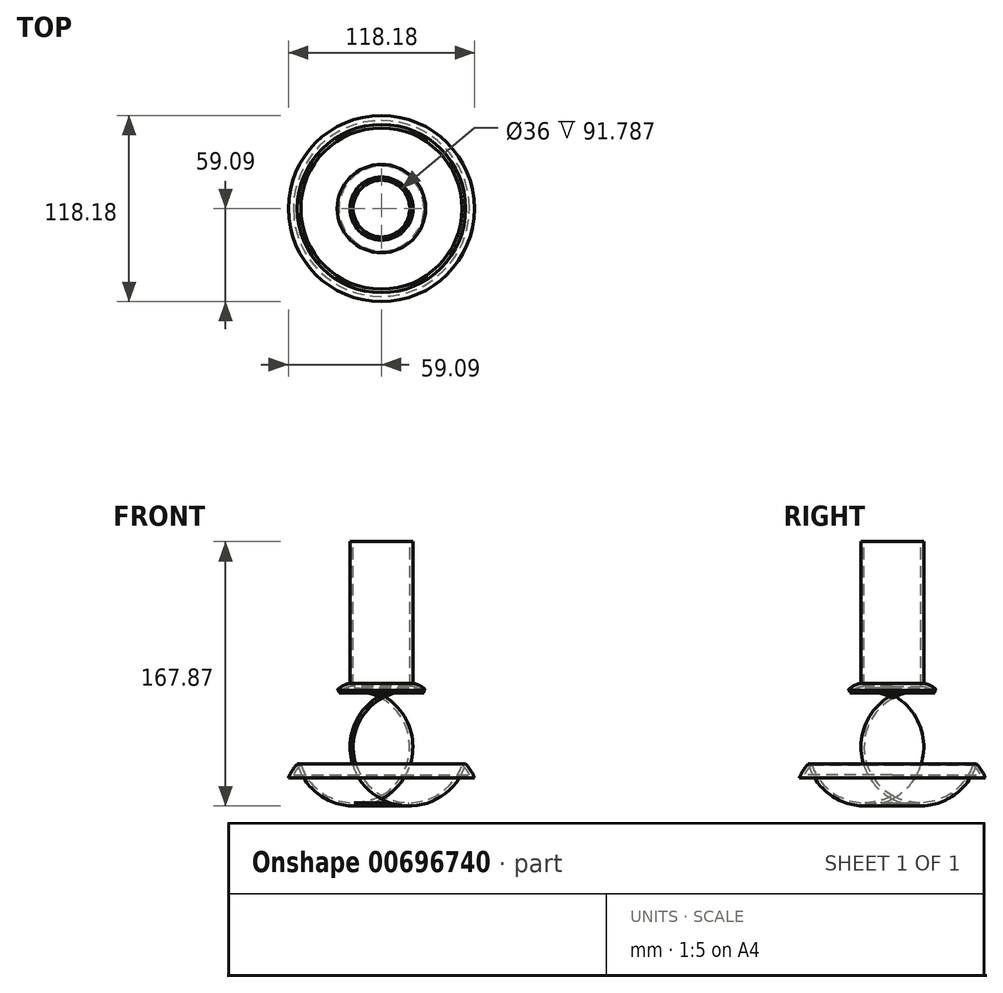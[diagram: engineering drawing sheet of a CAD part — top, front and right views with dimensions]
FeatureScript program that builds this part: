
annotation { "Feature Type Name" : "Feature", "Feature Type Description" : "" }
export const myFeature = defineFeature(function(context is Context, id is Id, definition is map)
    precondition{}
    {
        {
            var Q0;
            Q0=qCreatedBy(makeId("Front.planeOp"),FACE);
            var sketch = newSketch(context, id + "F0", { "sketchPlane" : qUnion([Q0])});
            skLineSegment(sketch, "E0", {"start": v(0, 90) * mm, "end": v(0, -60) * mm});
            skLineSegment(sketch, "E1", {"start": v(0, 90) * mm, "end": v(20, 90) * mm});
            skLineSegment(sketch, "E2", {"start": v(20, 90) * mm, "end": v(20, 0) * mm});
            skArc(sketch, "E3", {"start": v(28.08, -4.4) * mm, "mid": v(24.4, -1.55) * mm, "end": v(20, 0) * mm});
            skArc(sketch, "E4", {"start": v(53.44, -51.12) * mm, "mid": v(50.47, -22.5) * mm, "end": v(28.08, -4.4) * mm});
            skArc(sketch, "E5", {"start": v(59.09, -60) * mm, "mid": v(56.64, -55.32) * mm, "end": v(53.44, -51.12) * mm});
            skLineSegment(sketch, "E6", {"start": v(59.09, -60) * mm, "end": v(0, -60) * mm});
            skPoint(sketch, "E7", {"position": v(47.89, -18.4) * mm});
            skSolve(sketch);
        }
        {
            var Q0;
            Q0=makeQuery(id+"F0.imprint","IMPRINT",FACE,{"disambiguationData":[TD([[makeQuery(id+"F0.imprint","IMPRINT",EDGE,{"derivedFrom":sQuery(id+"F0.wireOp",EDGE,"E0")}),1.0]])]});
            var Q1;
            Q1=sQuery(id+"F0.wireOp",EDGE,"E0");
            revolve(context, id + "F1", {"entities" : qUnion([Q0]), "axis" : qUnion([Q1]), "revolveType" : RevolveType.FULL});
        }
        {
            var Q0;
            Q0=makeQuery(id+"F1.opRevolve","SWEPT_FACE",FACE,{"disambiguationData":[OSD([sQuery(id+"F0.wireOp",EDGE,"E1")])]});
            shell(context, id + "F2", {"entities" : qUnion([Q0]), "thickness" : 2 * mm});
        }
    });
